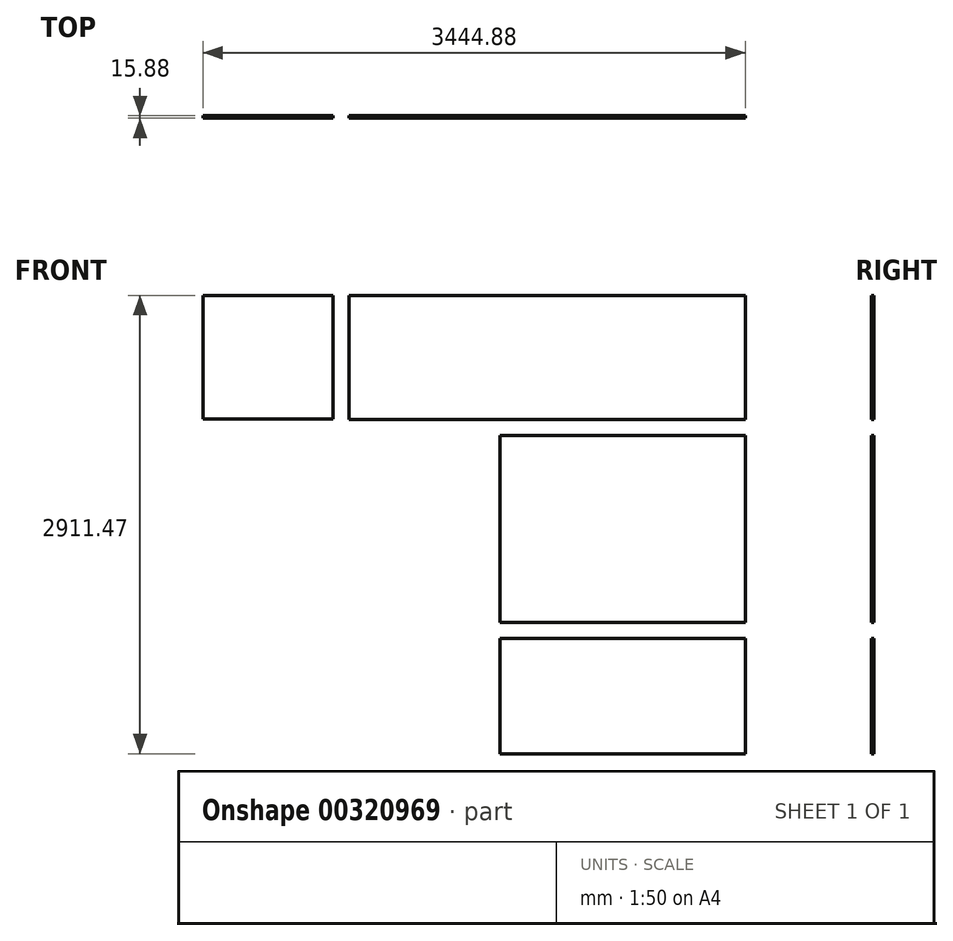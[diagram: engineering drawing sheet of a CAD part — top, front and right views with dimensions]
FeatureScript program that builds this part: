
annotation { "Feature Type Name" : "Feature", "Feature Type Description" : "" }
export const myFeature = defineFeature(function(context is Context, id is Id, definition is map)
    precondition{}
    {
        {
            var Q0;
            Q0=qCreatedBy(makeId("Front.planeOp"),FACE);
            var sketch = newSketch(context, id + "F0", { "sketchPlane" : qUnion([Q0])});
            skLineSegment(sketch, "E0.bottom", {"start": v(-825.5, 2911.47) * mm, "end": v(0, 2911.47) * mm});
            skLineSegment(sketch, "E0.top", {"start": v(-825.5, 2127.25) * mm, "end": v(0, 2127.25) * mm});
            skLineSegment(sketch, "E0.left", {"start": v(-825.5, 2911.47) * mm, "end": v(-825.5, 2127.25) * mm});
            skLineSegment(sketch, "E0.right", {"start": v(0, 2911.47) * mm, "end": v(0, 2127.25) * mm});
            skLineSegment(sketch, "E1.bottom", {"start": v(101.6, 2911.47) * mm, "end": v(2619.38, 2911.47) * mm});
            skLineSegment(sketch, "E1.top", {"start": v(101.6, 2124.07) * mm, "end": v(2619.38, 2124.07) * mm});
            skLineSegment(sketch, "E1.left", {"start": v(101.6, 2911.47) * mm, "end": v(101.6, 2124.07) * mm});
            skLineSegment(sketch, "E1.right", {"start": v(2619.38, 2911.48) * mm, "end": v(2619.38, 2124.07) * mm});
            skLineSegment(sketch, "E2.bottom", {"start": v(1060.45, 2022.47) * mm, "end": v(2619.38, 2022.47) * mm});
            skLineSegment(sketch, "E2.top", {"start": v(1060.45, 835.02) * mm, "end": v(2619.38, 835.03) * mm});
            skLineSegment(sketch, "E2.left", {"start": v(1060.45, 2022.47) * mm, "end": v(1060.45, 835.02) * mm});
            skLineSegment(sketch, "E2.right", {"start": v(2619.38, 2022.47) * mm, "end": v(2619.38, 835.03) * mm});
            skLineSegment(sketch, "E3.bottom", {"start": v(1060.45, 733.42) * mm, "end": v(2619.38, 733.43) * mm});
            skLineSegment(sketch, "E3.top", {"start": v(1060.45, 0) * mm, "end": v(2619.38, 0) * mm});
            skLineSegment(sketch, "E3.left", {"start": v(1060.45, 733.42) * mm, "end": v(1060.45, 0) * mm});
            skLineSegment(sketch, "E3.right", {"start": v(2619.38, 733.43) * mm, "end": v(2619.38, 0) * mm});
            skSolve(sketch);
        }
        {
            var Q0;
            Q0=makeQuery(id+"F0.imprint","IMPRINT",FACE,{"disambiguationData":[TD([[makeQuery(id+"F0.imprint","IMPRINT",EDGE,{"derivedFrom":sQuery(id+"F0.wireOp",EDGE,"E0.bottom")}),-1.0]])]});
            var Q1;
            Q1=makeQuery(id+"F0.imprint","IMPRINT",FACE,{"disambiguationData":[TD([[makeQuery(id+"F0.imprint","IMPRINT",EDGE,{"derivedFrom":sQuery(id+"F0.wireOp",EDGE,"E1.bottom")}),-1.0]])]});
            var Q2;
            Q2=makeQuery(id+"F0.imprint","IMPRINT",FACE,{"disambiguationData":[TD([[makeQuery(id+"F0.imprint","IMPRINT",EDGE,{"derivedFrom":sQuery(id+"F0.wireOp",EDGE,"E2.bottom")}),-1.0]])]});
            var Q3;
            Q3=makeQuery(id+"F0.imprint","IMPRINT",FACE,{"disambiguationData":[TD([[makeQuery(id+"F0.imprint","IMPRINT",EDGE,{"derivedFrom":sQuery(id+"F0.wireOp",EDGE,"E3.bottom")}),-1.0]])]});
            extrude(context, id + "F1", {"entities" : qUnion([Q0, Q1, Q2, Q3]), "depth" : 15.88 * mm});
        }
    });
